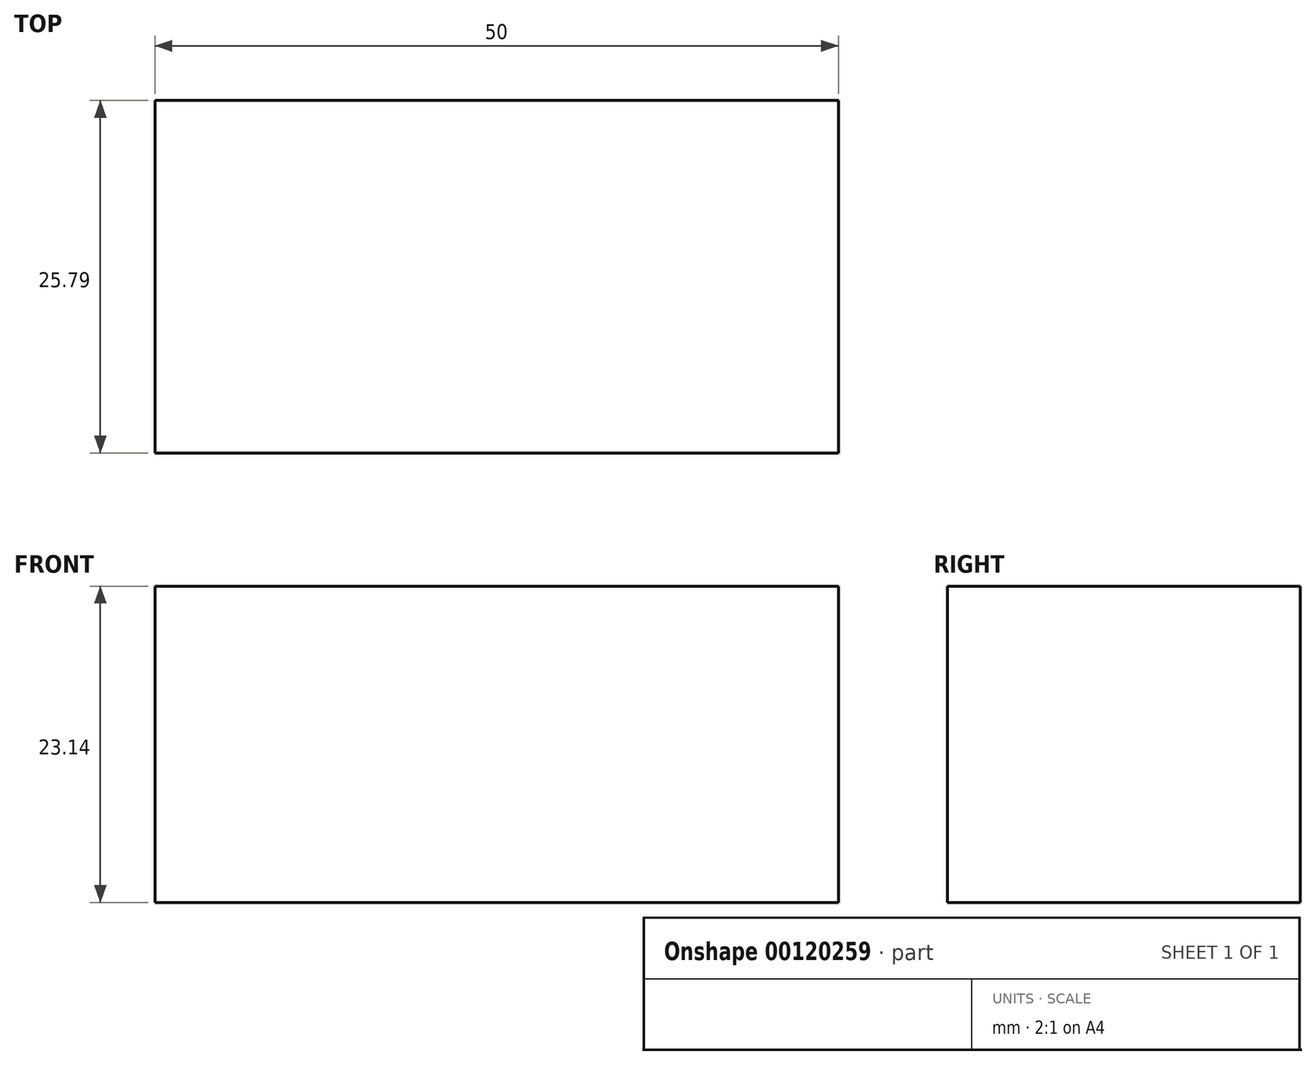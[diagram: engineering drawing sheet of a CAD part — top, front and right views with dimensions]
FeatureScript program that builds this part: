
annotation { "Feature Type Name" : "Feature", "Feature Type Description" : "" }
export const myFeature = defineFeature(function(context is Context, id is Id, definition is map)
    precondition{}
    {
        {
            var Q0;
            Q0=qCreatedBy(makeId("Right.planeOp"),FACE);
            cPlane(context, id + "F0", {"entities" : qUnion([Q0]), "cplaneType" : CPlaneType.OFFSET, "offset" : 10 * mm, "width" : 150 * mm, "height" : 150 * mm});
        }
        {
            var Q0;
            Q0=qCreatedBy(id+"F0.planeOp",FACE);
            var sketch = newSketch(context, id + "F1", { "sketchPlane" : qUnion([Q0])});
            skLineSegment(sketch, "E0.bottom", {"start": v(8.83, 64.21) * mm, "end": v(-16.96, 64.21) * mm});
            skLineSegment(sketch, "E0.top", {"start": v(8.83, 41.07) * mm, "end": v(-16.96, 41.07) * mm});
            skLineSegment(sketch, "E0.left", {"start": v(8.83, 64.21) * mm, "end": v(8.83, 41.07) * mm});
            skLineSegment(sketch, "E0.right", {"start": v(-16.96, 64.21) * mm, "end": v(-16.96, 41.07) * mm});
            skLineSegment(sketch, "E1", {"start": v(-4.07, 71.6) * mm, "end": v(-4.07, 34.5) * mm, "construction": true});
            skPoint(sketch, "E1.startSnap0", {"position": v(-4.07, 64.21) * mm});
            skPoint(sketch, "E1.endSnap0", {"position": v(-4.07, 41.07) * mm});
            skLineSegment(sketch, "E2", {"start": v(19.17, 52.64) * mm, "end": v(-23.97, 52.64) * mm, "construction": true});
            skPoint(sketch, "E2.startSnap0", {"position": v(8.83, 52.64) * mm});
            skPoint(sketch, "E2.endSnap0", {"position": v(-16.96, 52.64) * mm});
            skPoint(sketch, "E3", {"position": v(-4.07, 52.64) * mm});
            skSolve(sketch);
        }
        {
            var Q0;
            Q0 = qSketchRegion(id + "F1", true);
            extrude(context, id + "F2", {"entities" : qUnion([Q0]), "depth" : 50 * mm});
        }
    });
